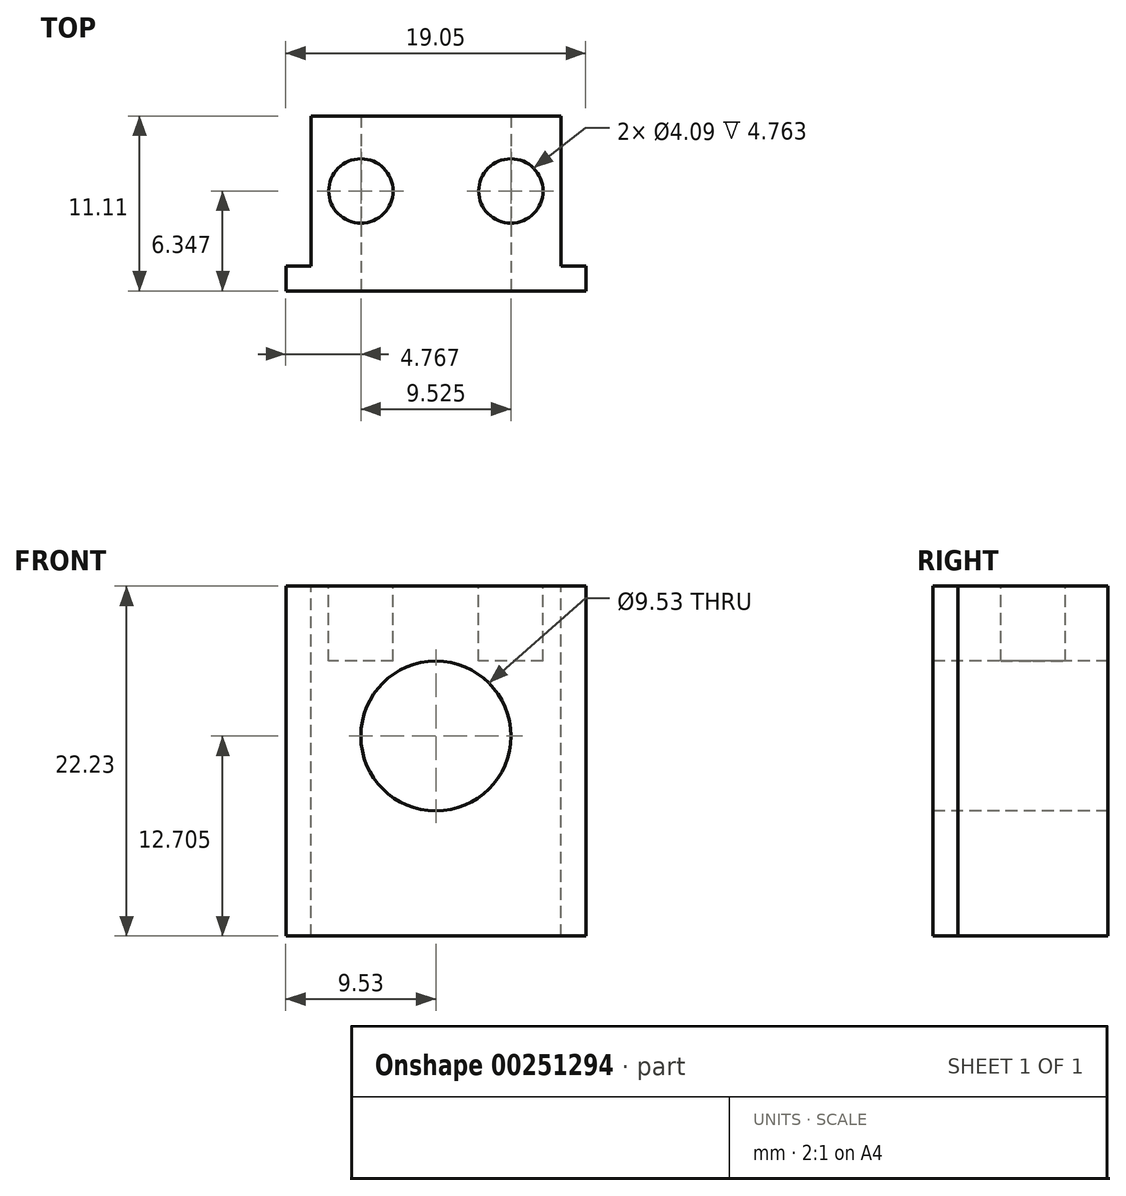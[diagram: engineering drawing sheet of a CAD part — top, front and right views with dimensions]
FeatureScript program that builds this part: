
annotation { "Feature Type Name" : "Feature", "Feature Type Description" : "" }
export const myFeature = defineFeature(function(context is Context, id is Id, definition is map)
    precondition{}
    {
        {
            var Q0;
            Q0=qCreatedBy(makeId("Front.planeOp"),FACE);
            var sketch = newSketch(context, id + "F0", { "sketchPlane" : qUnion([Q0])});
            skLineSegment(sketch, "E0.bottom", {"start": v(14.93, 36.79) * mm, "end": v(33.98, 36.79) * mm});
            skLineSegment(sketch, "E0.top", {"start": v(14.93, 14.56) * mm, "end": v(33.98, 14.56) * mm});
            skLineSegment(sketch, "E0.left", {"start": v(14.93, 36.79) * mm, "end": v(14.93, 14.56) * mm});
            skLineSegment(sketch, "E0.right", {"start": v(33.98, 36.79) * mm, "end": v(33.98, 14.56) * mm});
            skSolve(sketch);
        }
        {
            var Q0;
            Q0 = qSketchRegion(id + "F0", true);
            extrude(context, id + "F1", {"entities" : qUnion([Q0]), "depth" : 11.1 * mm});
        }
        {
            var Q0;
            Q0=makeQuery(id+"F1.opExtrude","SWEPT_FACE",FACE,{"disambiguationData":[OSD([sQuery(id+"F0.wireOp",EDGE,"E0.bottom")])]});
            var sketch = newSketch(context, id + "F2", { "sketchPlane" : qUnion([Q0])});
            skLineSegment(sketch, "E1", {"start": v(32.4, 0) * mm, "end": v(32.4, -9.53) * mm});
            skLineSegment(sketch, "E2", {"start": v(32.4, -9.53) * mm, "end": v(33.98, -9.53) * mm});
            skLineSegment(sketch, "E3", {"start": v(16.52, 0) * mm, "end": v(16.52, -9.53) * mm});
            skLineSegment(sketch, "E4", {"start": v(16.52, -9.53) * mm, "end": v(14.93, -9.53) * mm});
            skSolve(sketch);
        }
        {
            var Q0;
            Q0 = qSketchRegion(id + "F2", true);
            var Q1;
            {var subQ0=sQuery(id+"F2.wireOp",EDGE,"E3");Q1=makeQuery(id+"F2.imprint","IMPRINT",FACE,{"disambiguationData":[TD([[makeQuery(id+"F2.imprint","IMPRINT",EDGE,{"derivedFrom":subQ0}),-1.0]])]});}
            var Q2;
            {var subQ0=sQuery(id+"F2.wireOp",EDGE,"E1");Q2=makeQuery(id+"F2.imprint","IMPRINT",FACE,{"disambiguationData":[TD([[makeQuery(id+"F2.imprint","IMPRINT",EDGE,{"derivedFrom":subQ0}),1.0]])]});}
            extrude(context, id + "F3", {"entities" : qUnion([Q0, Q1, Q2]), "operationType" : NewBodyOperationType.REMOVE, "oppositeDirection" : true, "depth" : 25.4 * mm});
        }
        {
            var Q0;
            Q0=makeQuery(id+"F1.opExtrude","CAP_FACE",FACE,{"disambiguationData":[OSD([sQuery(id+"F0.wireOp",EDGE,"E0.bottom"),sQuery(id+"F0.wireOp",EDGE,"E0.top"),sQuery(id+"F0.wireOp",EDGE,"E0.left"),sQuery(id+"F0.wireOp",EDGE,"E0.right")])],"isStart":false});
            var sketch = newSketch(context, id + "F4", { "sketchPlane" : qUnion([Q0])});
            skCircle(sketch, "E5", {"center": v(24.46, 27.26) * mm, "radius": 4.76 * mm});
            skSolve(sketch);
        }
        {
            var Q0;
            Q0 = qSketchRegion(id + "F4", true);
            extrude(context, id + "F5", {"entities" : qUnion([Q0]), "operationType" : NewBodyOperationType.REMOVE, "oppositeDirection" : true, "depth" : 25.4 * mm});
        }
        {
            var Q0;
            Q0=makeQuery(id+"F1.opExtrude","SWEPT_FACE",FACE,{"disambiguationData":[OSD([sQuery(id+"F0.wireOp",EDGE,"E0.bottom")])]});
            var sketch = newSketch(context, id + "F6", { "sketchPlane" : qUnion([Q0])});
            skCircle(sketch, "E6", {"center": v(19.7, -4.76) * mm, "radius": 2.04 * mm});
            skCircle(sketch, "E7", {"center": v(29.22, -4.76) * mm, "radius": 2.04 * mm});
            skSolve(sketch);
        }
        {
            var Q0;
            Q0 = qSketchRegion(id + "F6", true);
            extrude(context, id + "F7", {"entities" : qUnion([Q0]), "operationType" : NewBodyOperationType.REMOVE, "oppositeDirection" : true, "depth" : 4.76 * mm});
        }
    });
